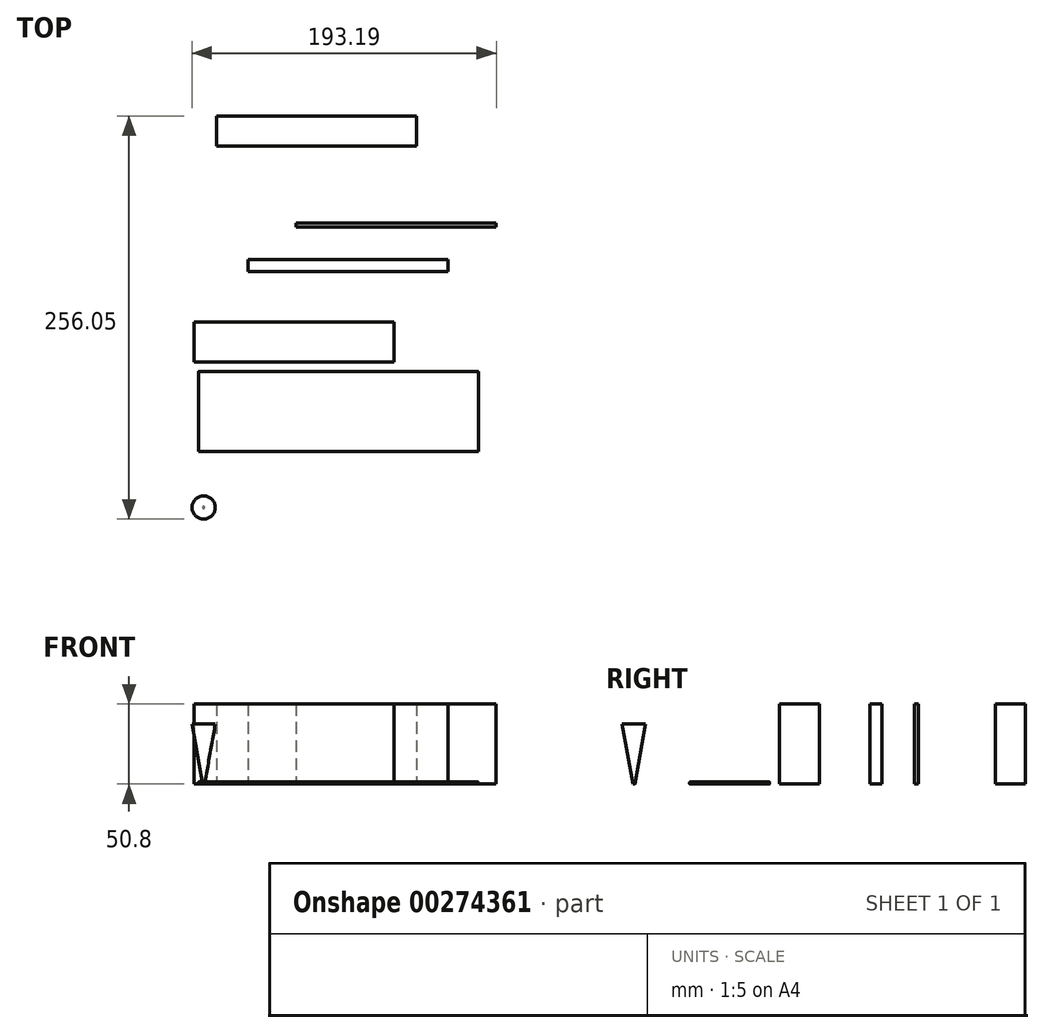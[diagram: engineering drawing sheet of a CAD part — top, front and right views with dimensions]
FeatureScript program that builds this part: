
annotation { "Feature Type Name" : "Feature", "Feature Type Description" : "" }
export const myFeature = defineFeature(function(context is Context, id is Id, definition is map)
    precondition{}
    {
        {
            var Q0;
            Q0=qCreatedBy(makeId("Top.planeOp"),FACE);
            var sketch = newSketch(context, id + "F0", { "sketchPlane" : qUnion([Q0])});
            skLineSegment(sketch, "E0.bottom", {"start": v(63.5, -12.7) * mm, "end": v(-63.5, -12.7) * mm});
            skLineSegment(sketch, "E0.top", {"start": v(63.5, 12.7) * mm, "end": v(-63.5, 12.7) * mm});
            skLineSegment(sketch, "E0.left", {"start": v(63.5, -12.7) * mm, "end": v(63.5, 12.7) * mm});
            skLineSegment(sketch, "E0.right", {"start": v(-63.5, -12.7) * mm, "end": v(-63.5, 12.7) * mm});
            skPoint(sketch, "E0.middle", {"position": v(0, 0) * mm});
            skLineSegment(sketch, "E1.bottom", {"start": v(-63.5, 12.7) * mm, "end": v(63.5, 12.7) * mm});
            skSolve(sketch);
        }
        {
            var Q0;
            Q0=makeQuery(id+"F0.imprint","IMPRINT",FACE,{"disambiguationData":[TD([[makeQuery(id+"F0.imprint","IMPRINT",EDGE,{"derivedFrom":sQuery(id+"F0.wireOp",EDGE,"E0.bottom")}),-1.0]])]});
            extrude(context, id + "F1", {"entities" : qUnion([Q0]), "depth" : 50.8 * mm});
        }
        {
            var Q0;
            Q0=qCreatedBy(makeId("Top.planeOp"),FACE);
            var sketch = newSketch(context, id + "F2", { "sketchPlane" : qUnion([Q0])});
            skLineSegment(sketch, "E2.bottom", {"start": v(-29.15, 52.33) * mm, "end": v(97.85, 52.33) * mm});
            skLineSegment(sketch, "E2.top", {"start": v(-29.15, 44.7) * mm, "end": v(97.85, 44.7) * mm});
            skLineSegment(sketch, "E2.left", {"start": v(-29.15, 52.33) * mm, "end": v(-29.15, 44.7) * mm});
            skLineSegment(sketch, "E2.right", {"start": v(97.85, 52.33) * mm, "end": v(97.85, 44.7) * mm});
            skSolve(sketch);
        }
        {
            var Q0;
            Q0=makeQuery(id+"F2.imprint","IMPRINT",FACE,{"disambiguationData":[TD([[makeQuery(id+"F2.imprint","IMPRINT",EDGE,{"derivedFrom":sQuery(id+"F2.wireOp",EDGE,"E2.bottom")}),-1.0]])]});
            extrude(context, id + "F3", {"entities" : qUnion([Q0]), "depth" : 50.8 * mm});
        }
        {
            var Q0;
            Q0=qCreatedBy(makeId("Top.planeOp"),FACE);
            var sketch = newSketch(context, id + "F4", { "sketchPlane" : qUnion([Q0])});
            skLineSegment(sketch, "E3.bottom", {"start": v(1.44, 73.1) * mm, "end": v(128.44, 73.1) * mm});
            skLineSegment(sketch, "E3.top", {"start": v(1.44, 75.64) * mm, "end": v(128.44, 75.64) * mm});
            skLineSegment(sketch, "E3.left", {"start": v(1.44, 73.1) * mm, "end": v(1.44, 75.64) * mm});
            skLineSegment(sketch, "E3.right", {"start": v(128.44, 73.1) * mm, "end": v(128.44, 75.64) * mm});
            skSolve(sketch);
        }
        {
            var Q0;
            Q0=makeQuery(id+"F4.imprint","IMPRINT",FACE,{"disambiguationData":[TD([[makeQuery(id+"F4.imprint","IMPRINT",EDGE,{"derivedFrom":sQuery(id+"F4.wireOp",EDGE,"E3.bottom")}),1.0]])]});
            extrude(context, id + "F5", {"entities" : qUnion([Q0]), "depth" : 50.8 * mm});
        }
        {
            var Q0;
            Q0=qCreatedBy(makeId("Top.planeOp"),FACE);
            var sketch = newSketch(context, id + "F6", { "sketchPlane" : qUnion([Q0])});
            skLineSegment(sketch, "E4.bottom", {"start": v(-49.1, 143.55) * mm, "end": v(77.9, 143.55) * mm});
            skLineSegment(sketch, "E4.top", {"start": v(-49.1, 124.5) * mm, "end": v(77.9, 124.5) * mm});
            skLineSegment(sketch, "E4.left", {"start": v(-49.1, 143.55) * mm, "end": v(-49.1, 124.5) * mm});
            skLineSegment(sketch, "E4.right", {"start": v(77.9, 143.55) * mm, "end": v(77.9, 124.5) * mm});
            skSolve(sketch);
        }
        {
            var Q0;
            Q0=makeQuery(id+"F6.imprint","IMPRINT",FACE,{"disambiguationData":[TD([[makeQuery(id+"F6.imprint","IMPRINT",EDGE,{"derivedFrom":sQuery(id+"F6.wireOp",EDGE,"E4.bottom")}),-1.0]])]});
            extrude(context, id + "F7", {"entities" : qUnion([Q0]), "depth" : 50.8 * mm});
        }
        {
            var Q0;
            Q0=qCreatedBy(makeId("Top.planeOp"),FACE);
            var sketch = newSketch(context, id + "F8", { "sketchPlane" : qUnion([Q0])});
            skLineSegment(sketch, "E5.bottom", {"start": v(-60.78, -18.85) * mm, "end": v(117.02, -18.85) * mm});
            skLineSegment(sketch, "E5.top", {"start": v(-60.78, -69.65) * mm, "end": v(117.02, -69.65) * mm});
            skLineSegment(sketch, "E5.left", {"start": v(-60.78, -18.85) * mm, "end": v(-60.78, -69.65) * mm});
            skLineSegment(sketch, "E5.right", {"start": v(117.02, -18.85) * mm, "end": v(117.02, -69.65) * mm});
            skSolve(sketch);
        }
        {
            var Q0;
            Q0=makeQuery(id+"F8.imprint","IMPRINT",FACE,{"disambiguationData":[TD([[makeQuery(id+"F8.imprint","IMPRINT",EDGE,{"derivedFrom":sQuery(id+"F8.wireOp",EDGE,"E5.bottom")}),-1.0]])]});
            extrude(context, id + "F9", {"entities" : qUnion([Q0]), "depth" : 1.27 * mm});
        }
        {
            var Q0;
            Q0=makeQuery(id+"F9.opExtrude","CAP_EDGE",EDGE,{"disambiguationData":[OSD([sQuery(id+"F8.wireOp",EDGE,"E5.bottom")])],"isStart":false});
            var Q1;
            Q1=makeQuery(id+"F9.opExtrude","CAP_EDGE",EDGE,{"disambiguationData":[OSD([sQuery(id+"F8.wireOp",EDGE,"E5.bottom")])],"isStart":true});
            var Q2;
            Q2=makeQuery(id+"F9.opExtrude","CAP_EDGE",EDGE,{"disambiguationData":[OSD([sQuery(id+"F8.wireOp",EDGE,"E5.left")])],"isStart":true});
            var Q3;
            Q3=makeQuery(id+"F9.opExtrude","CAP_EDGE",EDGE,{"disambiguationData":[OSD([sQuery(id+"F8.wireOp",EDGE,"E5.left")])],"isStart":false});
            var Q4;
            Q4=makeQuery(id+"F9.opExtrude","CAP_EDGE",EDGE,{"disambiguationData":[OSD([sQuery(id+"F8.wireOp",EDGE,"E5.top")])],"isStart":false});
            var Q5;
            Q5=makeQuery(id+"F9.opExtrude","CAP_EDGE",EDGE,{"disambiguationData":[OSD([sQuery(id+"F8.wireOp",EDGE,"E5.top")])],"isStart":true});
            var Q6;
            Q6=makeQuery(id+"F9.opExtrude","CAP_EDGE",EDGE,{"disambiguationData":[OSD([sQuery(id+"F8.wireOp",EDGE,"E5.right")])],"isStart":true});
            var Q7;
            Q7=makeQuery(id+"F9.opExtrude","CAP_EDGE",EDGE,{"disambiguationData":[OSD([sQuery(id+"F8.wireOp",EDGE,"E5.right")])],"isStart":false});
            fillet(context, id + "F10", {"entities" : qUnion([Q0, Q1, Q2, Q3, Q4, Q5, Q6, Q7]), "radius" : 0.25 * mm, "tangentPropagation" : true, "allowEdgeOverflow" : false});
        }
        {
            var Q0;
            Q0=qCreatedBy(makeId("Top.planeOp"),FACE);
            var sketch = newSketch(context, id + "F11", { "sketchPlane" : qUnion([Q0])});
            skCircle(sketch, "E6", {"center": v(-57.4, -105.15) * mm, "radius": 0.64 * mm});
            skSolve(sketch);
        }
        {
            var Q0;
            Q0=makeQuery(id+"F11.imprint","IMPRINT",FACE,{"disambiguationData":[TD([[makeQuery(id+"F11.imprint","IMPRINT",EDGE,{"derivedFrom":sQuery(id+"F11.wireOp",EDGE,"E6")}),1.0]])]});
            extrude(context, id + "F12", {"entities" : qUnion([Q0]), "depth" : 38.1 * mm, "hasDraft" : true, "draftAngle" : 10 * degree});
        }
    });
